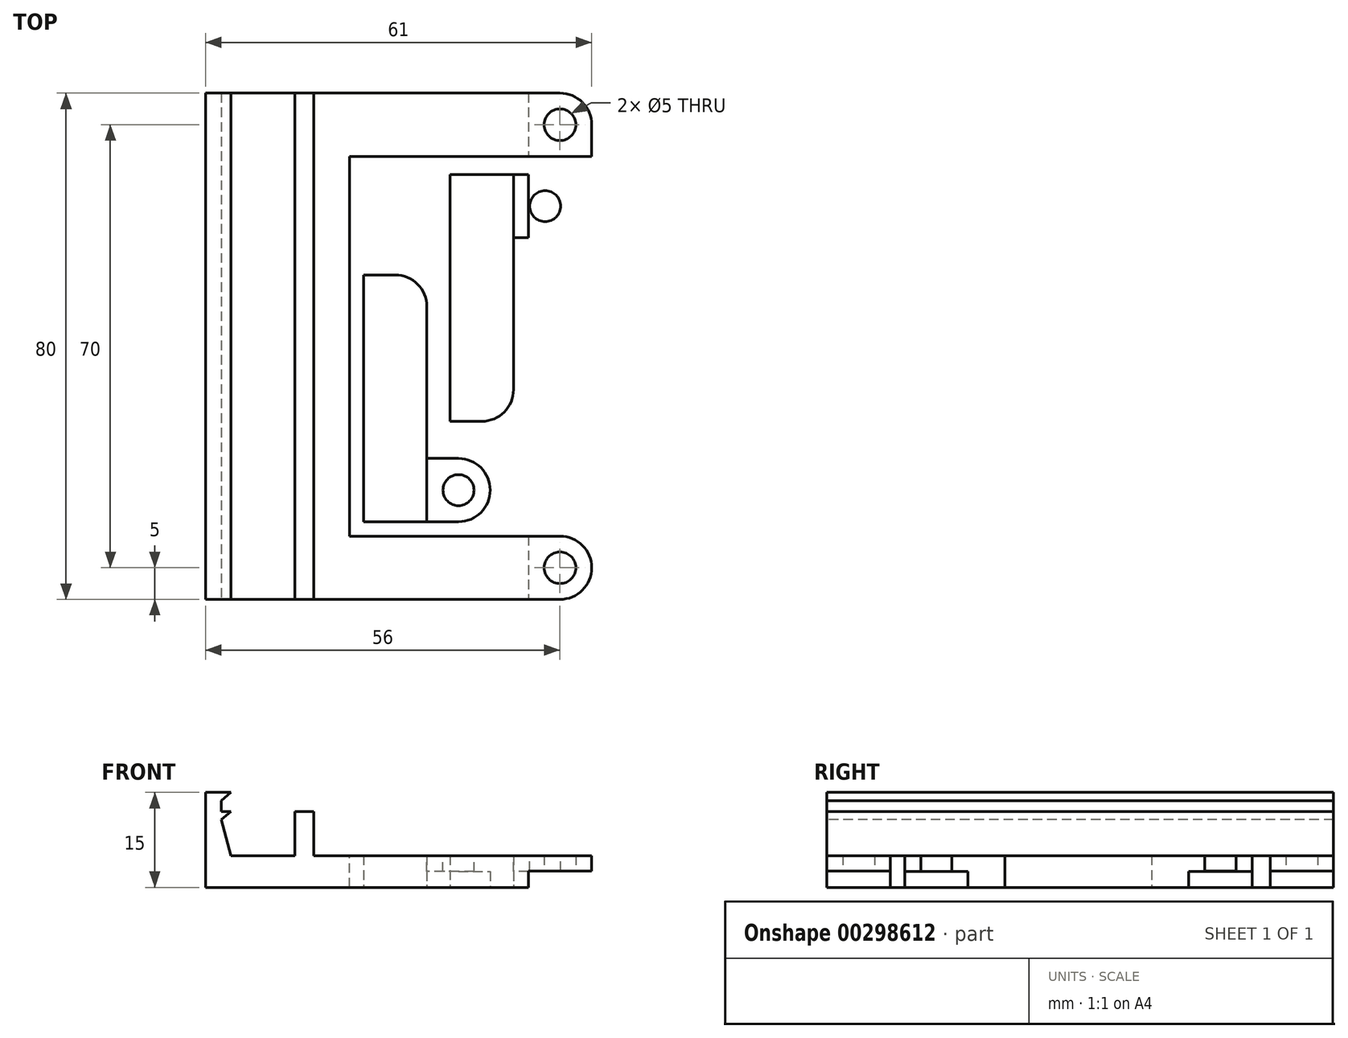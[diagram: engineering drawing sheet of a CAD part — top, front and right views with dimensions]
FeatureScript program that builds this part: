
annotation { "Feature Type Name" : "Feature", "Feature Type Description" : "" }
export const myFeature = defineFeature(function(context is Context, id is Id, definition is map)
    precondition{}
    {
        {
            var Q0;
            Q0=qCreatedBy(makeId("Top.planeOp"),FACE);
            var sketch = newSketch(context, id + "F0", { "sketchPlane" : qUnion([Q0])});
            skLineSegment(sketch, "E0", {"start": v(0, 0) * mm, "end": v(0, -40) * mm, "construction": true});
            skLineSegment(sketch, "E1.MirrorCS", {"start": v(0, 2.1) * mm, "end": v(0, 40) * mm, "construction": true});
            skLineSegment(sketch, "E2", {"start": v(0, 0) * mm, "end": v(50, 0) * mm});
            skLineSegment(sketch, "E3", {"start": v(0, 40) * mm, "end": v(50, 40) * mm});
            skLineSegment(sketch, "E4", {"start": v(50, 40) * mm, "end": v(50, -40) * mm});
            skLineSegment(sketch, "E5", {"start": v(50, -40) * mm, "end": v(0, -40) * mm});
            skLineSegment(sketch, "E6", {"start": v(0, 40) * mm, "end": v(-10, 40) * mm});
            skLineSegment(sketch, "E7", {"start": v(-10, 40) * mm, "end": v(-10, -40) * mm});
            skLineSegment(sketch, "E8", {"start": v(-10, -40) * mm, "end": v(0, -40) * mm});
            skLineSegment(sketch, "E9", {"start": v(45, 57.4) * mm, "end": v(45, -54.54) * mm, "construction": true});
            skLineSegment(sketch, "E10", {"start": v(-17.37, 35) * mm, "end": v(83.63, 35) * mm, "construction": true});
            skCircle(sketch, "E11", {"center": v(45, 35) * mm, "radius": 2.5 * mm});
            skCircle(sketch, "E12.MirrorC", {"center": v(45, -35) * mm, "radius": 2.5 * mm});
            skSolve(sketch);
        }
        {
            var Q0;
            Q0 = qSketchRegion(id + "F0", true);
            extrude(context, id + "F1", {"entities" : qUnion([Q0]), "depth" : 5 * mm});
        }
        {
            var Q0;
            Q0=makeQuery(id+"F1.opExtrude","CAP_FACE",FACE,{"disambiguationData":[OSD([sQuery(id+"F0.wireOp",EDGE,"E3"),sQuery(id+"F0.wireOp",EDGE,"E4"),sQuery(id+"F0.wireOp",EDGE,"E5"),sQuery(id+"F0.wireOp",EDGE,"E6"),sQuery(id+"F0.wireOp",EDGE,"E7"),sQuery(id+"F0.wireOp",EDGE,"E8")])],"isStart":false});
            var sketch = newSketch(context, id + "F2", { "sketchPlane" : qUnion([Q0])});
            skLineSegment(sketch, "E13", {"start": v(-10, 40) * mm, "end": v(-10, -40) * mm});
            skLineSegment(sketch, "E14", {"start": v(-7, 40) * mm, "end": v(-7, -40) * mm});
            skLineSegment(sketch, "E15", {"start": v(-10, 40) * mm, "end": v(-7, 40) * mm});
            skLineSegment(sketch, "E16", {"start": v(-10, -40) * mm, "end": v(-7, -40) * mm});
            skLineSegment(sketch, "E17.bottom", {"start": v(3.1, 40) * mm, "end": v(6.1, 40) * mm});
            skLineSegment(sketch, "E17.top", {"start": v(3.1, -40) * mm, "end": v(6.1, -40) * mm});
            skLineSegment(sketch, "E17.left", {"start": v(3.1, 40) * mm, "end": v(3.1, -40) * mm});
            skLineSegment(sketch, "E17.right", {"start": v(6.1, 40) * mm, "end": v(6.1, -40) * mm});
            skSolve(sketch);
        }
        {
            var Q0;
            Q0=makeQuery(id+"F2.imprint","IMPRINT",FACE,{"disambiguationData":[TD([[makeQuery(id+"F2.imprint","IMPRINT",EDGE,{"derivedFrom":sQuery(id+"F2.wireOp",EDGE,"E13")}),1.0]])]});
            var Q1;
            Q1=makeQuery(id+"F2.imprint","IMPRINT",FACE,{"disambiguationData":[TD([[makeQuery(id+"F2.imprint","IMPRINT",EDGE,{"derivedFrom":sQuery(id+"F2.wireOp",EDGE,"E17.bottom")}),-1.0]])]});
            extrude(context, id + "F3", {"entities" : qUnion([Q0, Q1]), "operationType" : NewBodyOperationType.ADD, "depth" : 7 * mm});
        }
        {
            var Q0;
            {var subQ0=sQuery(id+"F0.wireOp",EDGE,"E8");var subQ1=sQuery(id+"F0.wireOp",EDGE,"E5");var subQ2=sQuery(id+"F0.wireOp",EDGE,"E4");var subQ3=sQuery(id+"F0.wireOp",EDGE,"E6");var subQ4=sQuery(id+"F0.wireOp",EDGE,"E3");Q0=makeQuery(id+"F3.boolean.opBoolean","SPLIT",FACE,{"disambiguationData":[TD([makeQuery(id+"F1.opExtrude","SWEPT_FACE",FACE,{"disambiguationData":[OSD([subQ2])]})])],"derivedFrom":makeQuery(id+"F1.opExtrude","CAP_FACE",FACE,{"disambiguationData":[OSD([subQ4,subQ2,subQ1,subQ3,sQuery(id+"F0.wireOp",EDGE,"E7"),subQ0])],"isStart":false})});}
            var sketch = newSketch(context, id + "F4", { "sketchPlane" : qUnion([Q0])});
            skLineSegment(sketch, "E18.bottom", {"start": v(11.74, 30) * mm, "end": v(41.74, 30) * mm});
            skLineSegment(sketch, "E18.top", {"start": v(11.74, -30) * mm, "end": v(41.74, -30) * mm});
            skLineSegment(sketch, "E18.left", {"start": v(11.74, 30) * mm, "end": v(11.74, -30) * mm});
            skLineSegment(sketch, "E19", {"start": v(41.74, 30) * mm, "end": v(50, 30) * mm});
            skLineSegment(sketch, "E20", {"start": v(50, 30) * mm, "end": v(50, -30) * mm});
            skLineSegment(sketch, "E21", {"start": v(50, -30) * mm, "end": v(41.74, -30) * mm});
            skSolve(sketch);
        }
        {
            var Q0;
            Q0=makeQuery(id+"F4.imprint","IMPRINT",FACE,{"disambiguationData":[TD([[makeQuery(id+"F4.imprint","IMPRINT",EDGE,{"derivedFrom":sQuery(id+"F4.wireOp",EDGE,"E18.bottom")}),-1.0]])]});
            extrude(context, id + "F5", {"entities" : qUnion([Q0]), "operationType" : NewBodyOperationType.REMOVE, "oppositeDirection" : true, "depth" : 25 * mm});
        }
        {
            var Q0;
            Q0=makeQuery(id+"F3.boolean.opBoolean","MERGE",FACE,{"derivedFrom":[makeQuery(id+"F1.opExtrude","SWEPT_FACE",FACE,{"disambiguationData":[OSD([sQuery(id+"F0.wireOp",EDGE,"E5"),sQuery(id+"F0.wireOp",EDGE,"E8")])]}),makeQuery(id+"F3.opExtrude","SWEPT_FACE",FACE,{"disambiguationData":[OSD([sQuery(id+"F2.wireOp",EDGE,"E16")])]}),makeQuery(id+"F3.opExtrude","SWEPT_FACE",FACE,{"disambiguationData":[OSD([sQuery(id+"F2.wireOp",EDGE,"E17.top")])]})]});
            var sketch = newSketch(context, id + "F6", { "sketchPlane" : qUnion([Q0])});
            skLineSegment(sketch, "E22", {"start": v(-7, 12) * mm, "end": v(-8.5, 10.68) * mm});
            skLineSegment(sketch, "E23", {"start": v(-8.5, 10.68) * mm, "end": v(-7, 5) * mm});
            skLineSegment(sketch, "E24", {"start": v(-7, 12) * mm, "end": v(-7, 5) * mm});
            skSolve(sketch);
        }
        {
            var Q0;
            Q0=makeQuery(id+"F6.imprint","IMPRINT",FACE,{"disambiguationData":[TD([[makeQuery(id+"F6.imprint","IMPRINT",EDGE,{"derivedFrom":sQuery(id+"F6.wireOp",EDGE,"E22")}),1.0]])]});
            extrude(context, id + "F7", {"entities" : qUnion([Q0]), "operationType" : NewBodyOperationType.REMOVE, "oppositeDirection" : true, "depth" : 100 * mm});
        }
        {
            var Q0;
            Q0=makeQuery(id+"F3.boolean.opBoolean","MERGE",FACE,{"derivedFrom":[makeQuery(id+"F1.opExtrude","SWEPT_FACE",FACE,{"disambiguationData":[OSD([sQuery(id+"F0.wireOp",EDGE,"E7")])]}),makeQuery(id+"F3.opExtrude","SWEPT_FACE",FACE,{"disambiguationData":[OSD([sQuery(id+"F2.wireOp",EDGE,"E13")])]})]});
            extrude(context, id + "F8", {"entities" : qUnion([Q0]), "operationType" : NewBodyOperationType.ADD, "depth" : 1 * mm});
        }
        {
            var Q0;
            {var subQ0=sQuery(id+"F2.wireOp",EDGE,"E16");var subQ1=sQuery(id+"F0.wireOp",EDGE,"E8");Q0=makeQuery(id+"F8.boolean.opBoolean","MERGE",FACE,{"derivedFrom":[makeQuery(id+"F3.boolean.opBoolean","MERGE",FACE,{"derivedFrom":[makeQuery(id+"F1.opExtrude","SWEPT_FACE",FACE,{"disambiguationData":[OSD([sQuery(id+"F0.wireOp",EDGE,"E5"),subQ1])]}),makeQuery(id+"F3.opExtrude","SWEPT_FACE",FACE,{"disambiguationData":[OSD([subQ0])]}),makeQuery(id+"F3.opExtrude","SWEPT_FACE",FACE,{"disambiguationData":[OSD([sQuery(id+"F2.wireOp",EDGE,"E17.top")])]})]}),makeQuery(id+"F8.opExtrude","SWEPT_FACE",FACE,{"disambiguationData":[OSD([sQuery(id+"F0.wireOp",EDGE,"E7"),subQ1,sQuery(id+"F2.wireOp",EDGE,"E13"),subQ0])]})]});}
            var sketch = newSketch(context, id + "F9", { "sketchPlane" : qUnion([Q0])});
            skLineSegment(sketch, "E25.0.1.0", {"start": v(-11, 15) * mm, "end": v(-7, 15) * mm});
            skLineSegment(sketch, "E25.0.1.1", {"start": v(-7, 15) * mm, "end": v(-8.5, 13.68) * mm});
            skLineSegment(sketch, "E26", {"start": v(-11, 15) * mm, "end": v(-11, 12) * mm});
            skLineSegment(sketch, "E27", {"start": v(-11, 12) * mm, "end": v(-8.5, 12) * mm});
            skPoint(sketch, "E27.endSnap0", {"position": v(-9, 12) * mm});
            skLineSegment(sketch, "E28", {"start": v(-8.5, 12) * mm, "end": v(-8.5, 13.68) * mm});
            skSolve(sketch);
        }
        {
            var Q0;
            Q0=makeQuery(id+"F9.imprint","IMPRINT",FACE,{"disambiguationData":[TD([[makeQuery(id+"F9.imprint","IMPRINT",EDGE,{"derivedFrom":sQuery(id+"F9.wireOp",EDGE,"E25.0.1.0")}),-1.0]])]});
            extrude(context, id + "F10", {"entities" : qUnion([Q0]), "operationType" : NewBodyOperationType.ADD, "oppositeDirection" : true, "depth" : 80 * mm});
        }
        {
            var Q0;
            Q0=makeQuery(id+"F1.opExtrude","SWEPT_EDGE",EDGE,{"disambiguationData":[OSD([sQuery(id+"F0.wireOp",EDGE,"E3"),sQuery(id+"F0.wireOp",EDGE,"E4")])]});
            var Q1;
            Q1=makeQuery(id+"F5.boolean.opBoolean","COPY",EDGE,{"derivedFrom":makeQuery(id+"F5.opExtrude","SWEPT_EDGE",EDGE,{"disambiguationData":[OSD([sQuery(id+"F0.wireOp",EDGE,"E4"),sQuery(id+"F4.wireOp",EDGE,"E19"),sQuery(id+"F4.wireOp",EDGE,"E20")])]})});
            fillet(context, id + "F11", {"entities" : qUnion([Q0, Q1]), "radius" : 5 * mm, "tangentPropagation" : true, "allowEdgeOverflow" : false});
        }
        {
            var Q0;
            Q0=makeQuery(id+"F5.boolean.opBoolean","COPY",EDGE,{"derivedFrom":makeQuery(id+"F5.opExtrude","SWEPT_EDGE",EDGE,{"disambiguationData":[OSD([sQuery(id+"F0.wireOp",EDGE,"E4"),sQuery(id+"F4.wireOp",EDGE,"E20"),sQuery(id+"F4.wireOp",EDGE,"E21")])]})});
            var Q1;
            Q1=makeQuery(id+"F1.opExtrude","SWEPT_EDGE",EDGE,{"disambiguationData":[OSD([sQuery(id+"F0.wireOp",EDGE,"E4"),sQuery(id+"F0.wireOp",EDGE,"E5")])]});
            fillet(context, id + "F12", {"entities" : qUnion([Q0, Q1]), "radius" : 5 * mm, "tangentPropagation" : true, "allowEdgeOverflow" : false});
        }
        {
            var Q0;
            Q0=qCreatedBy(makeId("Top.planeOp"),FACE);
            var sketch = newSketch(context, id + "F13", { "sketchPlane" : qUnion([Q0])});
            skLineSegment(sketch, "E29.bottom", {"start": v(13.97, -27.74) * mm, "end": v(23.97, -27.74) * mm});
            skLineSegment(sketch, "E29.top", {"start": v(13.97, 11.26) * mm, "end": v(23.97, 11.26) * mm});
            skLineSegment(sketch, "E29.left", {"start": v(13.97, -27.74) * mm, "end": v(13.97, 11.26) * mm});
            skLineSegment(sketch, "E29.right", {"start": v(23.97, -17.74) * mm, "end": v(23.97, 11.26) * mm});
            skLineSegment(sketch, "E30", {"start": v(23.97, -27.74) * mm, "end": v(33.97, -27.74) * mm});
            skLineSegment(sketch, "E31", {"start": v(33.97, -27.74) * mm, "end": v(33.97, -17.74) * mm});
            skLineSegment(sketch, "E32", {"start": v(33.97, -17.74) * mm, "end": v(23.97, -17.74) * mm});
            skSolve(sketch);
        }
        {
            var Q0;
            Q0=makeQuery(id+"F13.imprint","IMPRINT",FACE,{"disambiguationData":[TD([[makeQuery(id+"F13.imprint","IMPRINT",EDGE,{"derivedFrom":sQuery(id+"F13.wireOp",EDGE,"E29.bottom")}),1.0]])]});
            extrude(context, id + "F14", {"entities" : qUnion([Q0]), "depth" : 5 * mm});
        }
        {
            var Q0;
            Q0=makeQuery(id+"F14.opExtrude","SWEPT_EDGE",EDGE,{"disambiguationData":[OSD([sQuery(id+"F13.wireOp",EDGE,"E30"),sQuery(id+"F13.wireOp",EDGE,"E31")])]});
            var Q1;
            Q1=makeQuery(id+"F14.opExtrude","SWEPT_EDGE",EDGE,{"disambiguationData":[OSD([sQuery(id+"F13.wireOp",EDGE,"E31"),sQuery(id+"F13.wireOp",EDGE,"E32")])]});
            fillet(context, id + "F15", {"entities" : qUnion([Q0, Q1]), "radius" : 5 * mm, "tangentPropagation" : true, "allowEdgeOverflow" : false});
        }
        {
            var Q0;
            Q0=makeQuery(id+"F14.opExtrude","CAP_FACE",FACE,{"disambiguationData":[OSD([sQuery(id+"F13.wireOp",EDGE,"E29.bottom"),sQuery(id+"F13.wireOp",EDGE,"E29.top"),sQuery(id+"F13.wireOp",EDGE,"E29.left"),sQuery(id+"F13.wireOp",EDGE,"E29.right"),sQuery(id+"F13.wireOp",EDGE,"E30"),sQuery(id+"F13.wireOp",EDGE,"E31"),sQuery(id+"F13.wireOp",EDGE,"E32")])],"isStart":false});
            var sketch = newSketch(context, id + "F16", { "sketchPlane" : qUnion([Q0])});
            skPoint(sketch, "E33.endSnap0", {"position": v(33.97, -22.74) * mm});
            skPoint(sketch, "E34.endSnap0", {"position": v(23.97, -22.74) * mm});
            skLineSegment(sketch, "E35", {"start": v(23.97, -17.74) * mm, "end": v(23.97, -27.74) * mm});
            skLineSegment(sketch, "E36", {"start": v(23.97, -27.74) * mm, "end": v(33.97, -27.74) * mm});
            skLineSegment(sketch, "E37", {"start": v(33.97, -27.74) * mm, "end": v(33.97, -17.74) * mm});
            skPoint(sketch, "E37.endSnap0", {"position": v(26.47, -17.74) * mm});
            skLineSegment(sketch, "E38", {"start": v(33.97, -17.74) * mm, "end": v(23.97, -17.74) * mm});
            skCircle(sketch, "E39", {"center": v(28.97, -22.74) * mm, "radius": 2.45 * mm});
            skSolve(sketch);
        }
        {
            var Q0;
            {var subQ1=sQuery(id+"F16.wireOp",EDGE,"E35");Q0=makeQuery(id+"F16.imprint","IMPRINT",FACE,{"disambiguationData":[TD([[makeQuery(id+"F16.imprint","IMPRINT",EDGE,{"derivedFrom":subQ1}),1.0]])]});}
            extrude(context, id + "F17", {"entities" : qUnion([Q0]), "operationType" : NewBodyOperationType.REMOVE, "oppositeDirection" : true, "depth" : 2.5 * mm});
        }
        {
            var Q0;
            Q0=makeQuery(id+"F14.opExtrude","SWEPT_EDGE",EDGE,{"disambiguationData":[OSD([sQuery(id+"F13.wireOp",EDGE,"E29.top"),sQuery(id+"F13.wireOp",EDGE,"E29.right")])]});
            fillet(context, id + "F18", {"entities" : qUnion([Q0]), "radius" : 5 * mm, "tangentPropagation" : true, "allowEdgeOverflow" : false});
        }
        {
            var Q0;
            Q0=qCreatedBy(makeId("Front.planeOp"),FACE);
            var sketch = newSketch(context, id + "F19", { "sketchPlane" : qUnion([Q0])});
            skLineSegment(sketch, "E40", {"start": v(29.66, 24.63) * mm, "end": v(29.66, -22.77) * mm, "construction": true});
            skSolve(sketch);
        }
        {
            var Q0;
            Q0=makeQuery(id+"F14.opExtrude","SWEPT_BODY",BODY,{"disambiguationData":[OSD([sQuery(id+"F13.wireOp",EDGE,"E29.bottom"),sQuery(id+"F13.wireOp",EDGE,"E29.top"),sQuery(id+"F13.wireOp",EDGE,"E29.left"),sQuery(id+"F13.wireOp",EDGE,"E29.right"),sQuery(id+"F13.wireOp",EDGE,"E30"),sQuery(id+"F13.wireOp",EDGE,"E31"),sQuery(id+"F13.wireOp",EDGE,"E32")])]});
            var Q1;
            Q1=sQuery(id+"F19.wireOp",EDGE,"E40");
            transform(context, id + "F20", {"entities" : qUnion([Q0]), "transformType" : TransformType.ROTATION, "transformAxis" : qUnion([Q1]), "angle" : 180 * degree, "makeCopy" : true});
        }
        {
            var Q0;
            Q0=makeQuery(id+"F20.opPattern","COPY",BODY,{"derivedFrom":makeQuery(id+"F14.opExtrude","SWEPT_BODY",BODY,{"disambiguationData":[OSD([sQuery(id+"F13.wireOp",EDGE,"E29.bottom"),sQuery(id+"F13.wireOp",EDGE,"E29.top"),sQuery(id+"F13.wireOp",EDGE,"E29.left"),sQuery(id+"F13.wireOp",EDGE,"E29.right"),sQuery(id+"F13.wireOp",EDGE,"E30"),sQuery(id+"F13.wireOp",EDGE,"E31"),sQuery(id+"F13.wireOp",EDGE,"E32")])]}),"instanceName":"1"});
            var Q1;
            Q1=qCreatedBy(makeId("Right.planeOp"),FACE);
            mirror(context, id + "F21", {"entities" : qUnion([Q0]), "mirrorPlane" : qUnion([Q1])});
        }
        {
            var Q0;
            Q0=makeQuery(id+"F20.opPattern","COPY",BODY,{"derivedFrom":makeQuery(id+"F14.opExtrude","SWEPT_BODY",BODY,{"disambiguationData":[OSD([sQuery(id+"F13.wireOp",EDGE,"E29.bottom"),sQuery(id+"F13.wireOp",EDGE,"E29.top"),sQuery(id+"F13.wireOp",EDGE,"E29.left"),sQuery(id+"F13.wireOp",EDGE,"E29.right"),sQuery(id+"F13.wireOp",EDGE,"E30"),sQuery(id+"F13.wireOp",EDGE,"E31"),sQuery(id+"F13.wireOp",EDGE,"E32")])]}),"instanceName":"1"});
            deleteBodies(context, id + "F22", {"entities" : qUnion([Q0])});
        }
        {
            var Q0;
            Q0=makeQuery(id+"F21.opPattern","COPY",BODY,{"derivedFrom":makeQuery(id+"F20.opPattern","COPY",BODY,{"derivedFrom":makeQuery(id+"F14.opExtrude","SWEPT_BODY",BODY,{"disambiguationData":[OSD([sQuery(id+"F13.wireOp",EDGE,"E29.bottom"),sQuery(id+"F13.wireOp",EDGE,"E29.top"),sQuery(id+"F13.wireOp",EDGE,"E29.left"),sQuery(id+"F13.wireOp",EDGE,"E29.right"),sQuery(id+"F13.wireOp",EDGE,"E30"),sQuery(id+"F13.wireOp",EDGE,"E31"),sQuery(id+"F13.wireOp",EDGE,"E32")])]}),"instanceName":"1"}),"instanceName":"1"});
            var Q1;
            Q1=sQuery(id+"F0.wireOp",EDGE,"E2");
            transform(context, id + "F23", {"entities" : qUnion([Q0]), "transformType" : TransformType.TRANSLATION_3D, "dx" : 73 * mm, "dy" : -0.6 * mm, "dz" : 0 * mm, "makeCopy" : false});
        }
        {
            var Q0;
            {var subQ0=sQuery(id+"F2.wireOp",EDGE,"E16");var subQ1=sQuery(id+"F0.wireOp",EDGE,"E8");Q0=makeQuery(id+"F10.boolean.opBoolean","MERGE",FACE,{"derivedFrom":[makeQuery(id+"F8.boolean.opBoolean","MERGE",FACE,{"derivedFrom":[makeQuery(id+"F3.boolean.opBoolean","MERGE",FACE,{"derivedFrom":[makeQuery(id+"F1.opExtrude","SWEPT_FACE",FACE,{"disambiguationData":[OSD([sQuery(id+"F0.wireOp",EDGE,"E5"),subQ1])]}),makeQuery(id+"F3.opExtrude","SWEPT_FACE",FACE,{"disambiguationData":[OSD([subQ0])]}),makeQuery(id+"F3.opExtrude","SWEPT_FACE",FACE,{"disambiguationData":[OSD([sQuery(id+"F2.wireOp",EDGE,"E17.top")])]})]}),makeQuery(id+"F8.opExtrude","SWEPT_FACE",FACE,{"disambiguationData":[OSD([sQuery(id+"F0.wireOp",EDGE,"E7"),subQ1,sQuery(id+"F2.wireOp",EDGE,"E13"),subQ0])]})]}),makeQuery(id+"F10.opExtrude","CAP_FACE",FACE,{"disambiguationData":[OSD([sQuery(id+"F9.wireOp",EDGE,"E25.0.1.0"),sQuery(id+"F9.wireOp",EDGE,"E25.0.1.1"),sQuery(id+"F9.wireOp",EDGE,"E26"),sQuery(id+"F9.wireOp",EDGE,"E27"),sQuery(id+"F9.wireOp",EDGE,"E28")])],"isStart":true})]});}
            var sketch = newSketch(context, id + "F24", { "sketchPlane" : qUnion([Q0])});
            skLineSegment(sketch, "E41", {"start": v(45, 0) * mm, "end": v(50, 0) * mm});
            skLineSegment(sketch, "E42", {"start": v(45, 0) * mm, "end": v(40, 0) * mm});
            skLineSegment(sketch, "E43", {"start": v(40, 0) * mm, "end": v(40, 2.6) * mm});
            skLineSegment(sketch, "E44", {"start": v(40, 2.6) * mm, "end": v(50, 2.6) * mm});
            skLineSegment(sketch, "E45", {"start": v(50, 2.6) * mm, "end": v(50, 0) * mm});
            skSolve(sketch);
        }
        {
            var Q0;
            {var subQ0=sQuery(id+"F24.wireOp",EDGE,"E42");Q0=makeQuery(id+"F24.imprint","IMPRINT",FACE,{"disambiguationData":[TD([[makeQuery(id+"F24.imprint","IMPRINT",EDGE,{"derivedFrom":subQ0}),1.0]])]});}
            var Q1;
            {var subQ0=sQuery(id+"F24.wireOp",EDGE,"E41");Q1=makeQuery(id+"F24.imprint","IMPRINT",FACE,{"disambiguationData":[TD([[makeQuery(id+"F24.imprint","IMPRINT",EDGE,{"derivedFrom":subQ0}),1.0]])]});}
            extrude(context, id + "F25", {"entities" : qUnion([Q0, Q1]), "operationType" : NewBodyOperationType.REMOVE, "oppositeDirection" : true, "depth" : 100 * mm});
        }
    });
